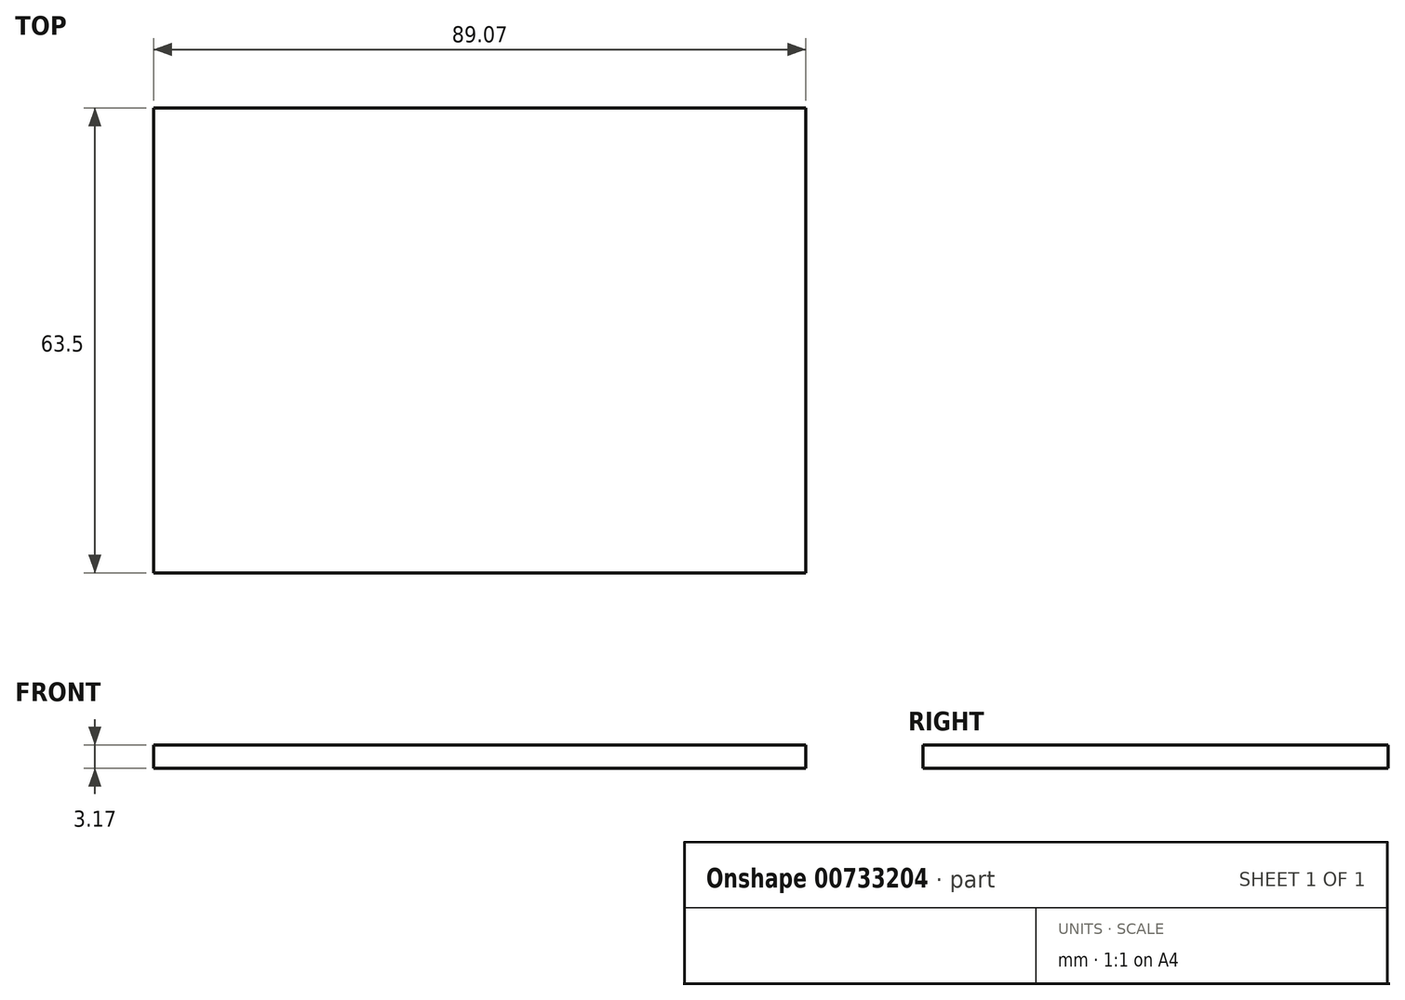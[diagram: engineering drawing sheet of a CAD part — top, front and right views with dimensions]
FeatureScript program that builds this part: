
annotation { "Feature Type Name" : "Feature", "Feature Type Description" : "" }
export const myFeature = defineFeature(function(context is Context, id is Id, definition is map)
    precondition{}
    {
        {
            var Q0;
            Q0=qCreatedBy(makeId("Top.planeOp"),FACE);
            var sketch = newSketch(context, id + "F0", { "sketchPlane" : qUnion([Q0])});
            skLineSegment(sketch, "E0.bottom", {"start": v(-31.53, 17.86) * mm, "end": v(44.67, 17.86) * mm});
            skLineSegment(sketch, "E0.top", {"start": v(-31.53, -32.94) * mm, "end": v(44.67, -32.94) * mm});
            skLineSegment(sketch, "E0.left", {"start": v(-31.53, 17.86) * mm, "end": v(-31.53, -32.94) * mm});
            skLineSegment(sketch, "E0.right", {"start": v(44.67, 17.86) * mm, "end": v(44.67, -32.94) * mm});
            skCircle(sketch, "E1", {"center": v(-31.53, 17.86) * mm, "radius": 6.35 * mm});
            skCircle(sketch, "E2", {"center": v(-31.53, -32.94) * mm, "radius": 6.35 * mm});
            skCircle(sketch, "E3", {"center": v(44.67, 17.86) * mm, "radius": 6.35 * mm});
            skCircle(sketch, "E4", {"center": v(44.67, -32.94) * mm, "radius": 6.35 * mm});
            skLineSegment(sketch, "E5.bottom", {"start": v(-38.05, -39.29) * mm, "end": v(51.02, -39.29) * mm});
            skLineSegment(sketch, "E5.top", {"start": v(-38.05, 24.21) * mm, "end": v(51.02, 24.21) * mm});
            skLineSegment(sketch, "E5.left", {"start": v(-38.05, -39.29) * mm, "end": v(-38.05, 24.21) * mm});
            skLineSegment(sketch, "E5.right", {"start": v(51.02, -39.29) * mm, "end": v(51.02, 24.21) * mm});
            skSolve(sketch);
        }
        {
            var Q0;
            {var subQ5=sQuery(id+"F0.wireOp",EDGE,"E1");var subQ13=sQuery(id+"F0.wireOp",EDGE,"E0.bottom");var subQ14=makeQuery(id+"F0.imprint","INTERSECT",VERTEX,{"derivedFrom":[subQ13,subQ5]});Q0=makeQuery(id+"F0.imprint","IMPRINT",FACE,{"disambiguationData":[TD([[makeQuery(id+"F0.imprint","IMPRINT",EDGE,{"disambiguationData":[TD([[subQ14,-1.0]])],"derivedFrom":subQ13}),-1.0]])]});}
            var Q1;
            {var subQ0=sQuery(id+"F0.wireOp",EDGE,"E0.left");var subQ1=sQuery(id+"F0.wireOp",EDGE,"E0.bottom");var subQ2=makeQuery(id+"F0.imprint","INTERSECT",VERTEX,{"derivedFrom":[subQ1,subQ0]});Q1=makeQuery(id+"F0.imprint","IMPRINT",FACE,{"disambiguationData":[TD([[makeQuery(id+"F0.imprint","IMPRINT",EDGE,{"disambiguationData":[TD([[subQ2,-1.0]])],"derivedFrom":subQ1}),1.0]])]});}
            var Q2;
            {var subQ0=sQuery(id+"F0.wireOp",EDGE,"E0.left");var subQ1=sQuery(id+"F0.wireOp",EDGE,"E0.top");var subQ2=makeQuery(id+"F0.imprint","INTERSECT",VERTEX,{"derivedFrom":[subQ1,subQ0]});Q2=makeQuery(id+"F0.imprint","IMPRINT",FACE,{"disambiguationData":[TD([[makeQuery(id+"F0.imprint","IMPRINT",EDGE,{"disambiguationData":[TD([[subQ2,-1.0]])],"derivedFrom":subQ1}),-1.0]])]});}
            var Q3;
            {var subQ2=sQuery(id+"F0.wireOp",EDGE,"E0.top");var subQ5=sQuery(id+"F0.wireOp",EDGE,"E0.right");var subQ7=makeQuery(id+"F0.imprint","INTERSECT",VERTEX,{"derivedFrom":[subQ2,subQ5]});Q3=makeQuery(id+"F0.imprint","IMPRINT",FACE,{"disambiguationData":[TD([[makeQuery(id+"F0.imprint","IMPRINT",EDGE,{"disambiguationData":[TD([[subQ7,1.0]])],"derivedFrom":subQ2}),-1.0]])]});}
            var Q4;
            {var subQ3=sQuery(id+"F0.wireOp",EDGE,"E0.bottom");var subQ5=sQuery(id+"F0.wireOp",EDGE,"E0.right");var subQ6=makeQuery(id+"F0.imprint","INTERSECT",VERTEX,{"derivedFrom":[subQ3,subQ5]});Q4=makeQuery(id+"F0.imprint","IMPRINT",FACE,{"disambiguationData":[TD([[makeQuery(id+"F0.imprint","IMPRINT",EDGE,{"disambiguationData":[TD([[subQ6,1.0]])],"derivedFrom":subQ3}),1.0]])]});}
            var Q5;
            {var subQ0=sQuery(id+"F0.wireOp",EDGE,"E3");var subQ1=sQuery(id+"F0.wireOp",EDGE,"E0.right");var subQ2=makeQuery(id+"F0.imprint","INTERSECT",VERTEX,{"derivedFrom":[subQ1,subQ0]});Q5=makeQuery(id+"F0.imprint","IMPRINT",FACE,{"disambiguationData":[TD([[makeQuery(id+"F0.imprint","IMPRINT",EDGE,{"disambiguationData":[TD([[subQ2,-1.0]])],"derivedFrom":subQ1}),1.0]])]});}
            var Q6;
            {var subQ0=sQuery(id+"F0.wireOp",EDGE,"E2");var subQ1=sQuery(id+"F0.wireOp",EDGE,"E0.top");var subQ2=makeQuery(id+"F0.imprint","INTERSECT",VERTEX,{"derivedFrom":[subQ1,subQ0]});Q6=makeQuery(id+"F0.imprint","IMPRINT",FACE,{"disambiguationData":[TD([[makeQuery(id+"F0.imprint","IMPRINT",EDGE,{"disambiguationData":[TD([[subQ2,-1.0]])],"derivedFrom":subQ1}),-1.0]])]});}
            var Q7;
            {var subQ0=sQuery(id+"F0.wireOp",EDGE,"E5.left");Q7=makeQuery(id+"F0.imprint","IMPRINT",FACE,{"disambiguationData":[TD([[makeQuery(id+"F0.imprint","IMPRINT",EDGE,{"derivedFrom":subQ0}),-1.0]])]});}
            var Q8;
            {var subQ0=sQuery(id+"F0.wireOp",EDGE,"E1");var subQ1=sQuery(id+"F0.wireOp",EDGE,"E0.bottom");var subQ2=makeQuery(id+"F0.imprint","INTERSECT",VERTEX,{"derivedFrom":[subQ1,subQ0]});Q8=makeQuery(id+"F0.imprint","IMPRINT",FACE,{"disambiguationData":[TD([[makeQuery(id+"F0.imprint","IMPRINT",EDGE,{"disambiguationData":[TD([[subQ2,-1.0]])],"derivedFrom":subQ1}),1.0]])]});}
            var Q9;
            {var subQ0=sQuery(id+"F0.wireOp",EDGE,"E0.right");var subQ1=sQuery(id+"F0.wireOp",EDGE,"E0.bottom");var subQ2=makeQuery(id+"F0.imprint","INTERSECT",VERTEX,{"derivedFrom":[subQ1,subQ0]});Q9=makeQuery(id+"F0.imprint","IMPRINT",FACE,{"disambiguationData":[TD([[makeQuery(id+"F0.imprint","IMPRINT",EDGE,{"disambiguationData":[TD([[subQ2,1.0]])],"derivedFrom":subQ1}),-1.0]])]});}
            var Q10;
            {var subQ0=sQuery(id+"F0.wireOp",EDGE,"E0.right");var subQ1=sQuery(id+"F0.wireOp",EDGE,"E0.top");var subQ2=makeQuery(id+"F0.imprint","INTERSECT",VERTEX,{"derivedFrom":[subQ1,subQ0]});Q10=makeQuery(id+"F0.imprint","IMPRINT",FACE,{"disambiguationData":[TD([[makeQuery(id+"F0.imprint","IMPRINT",EDGE,{"disambiguationData":[TD([[subQ2,1.0]])],"derivedFrom":subQ1}),1.0]])]});}
            var Q11;
            {var subQ0=sQuery(id+"F0.wireOp",EDGE,"E0.left");var subQ1=sQuery(id+"F0.wireOp",EDGE,"E0.top");var subQ2=makeQuery(id+"F0.imprint","INTERSECT",VERTEX,{"derivedFrom":[subQ1,subQ0]});Q11=makeQuery(id+"F0.imprint","IMPRINT",FACE,{"disambiguationData":[TD([[makeQuery(id+"F0.imprint","IMPRINT",EDGE,{"disambiguationData":[TD([[subQ2,-1.0]])],"derivedFrom":subQ1}),1.0]])]});}
            var Q12;
            {var subQ0=sQuery(id+"F0.wireOp",EDGE,"E0.left");var subQ1=sQuery(id+"F0.wireOp",EDGE,"E0.bottom");var subQ2=makeQuery(id+"F0.imprint","INTERSECT",VERTEX,{"derivedFrom":[subQ1,subQ0]});Q12=makeQuery(id+"F0.imprint","IMPRINT",FACE,{"disambiguationData":[TD([[makeQuery(id+"F0.imprint","IMPRINT",EDGE,{"disambiguationData":[TD([[subQ2,-1.0]])],"derivedFrom":subQ1}),-1.0]])]});}
            var Q13;
            {var subQ0=sQuery(id+"F0.wireOp",EDGE,"E5.top");var subQ1=sQuery(id+"F0.wireOp",EDGE,"E3");var subQ2=makeQuery(id+"F0.imprint","INTERSECT",VERTEX,{"derivedFrom":[subQ1,subQ0]});Q13=makeQuery(id+"F0.imprint","IMPRINT",FACE,{"disambiguationData":[TD([[makeQuery(id+"F0.imprint","IMPRINT",EDGE,{"disambiguationData":[TD([[subQ2,1.0]])],"derivedFrom":subQ1}),-1.0]])]});}
            var Q14;
            {var subQ0=sQuery(id+"F0.wireOp",EDGE,"E5.right");var subQ1=sQuery(id+"F0.wireOp",EDGE,"E4");var subQ2=makeQuery(id+"F0.imprint","INTERSECT",VERTEX,{"derivedFrom":[subQ1,subQ0]});Q14=makeQuery(id+"F0.imprint","IMPRINT",FACE,{"disambiguationData":[TD([[makeQuery(id+"F0.imprint","IMPRINT",EDGE,{"disambiguationData":[TD([[subQ2,1.0]])],"derivedFrom":subQ1}),-1.0]])]});}
            extrude(context, id + "F1", {"entities" : qUnion([Q0, Q1, Q2, Q3, Q4, Q5, Q6, Q7, Q8, Q9, Q10, Q11, Q12, Q13, Q14]), "depth" : 3.17 * mm, "offsetDistance" : 25.4 * mm});
        }
    });
